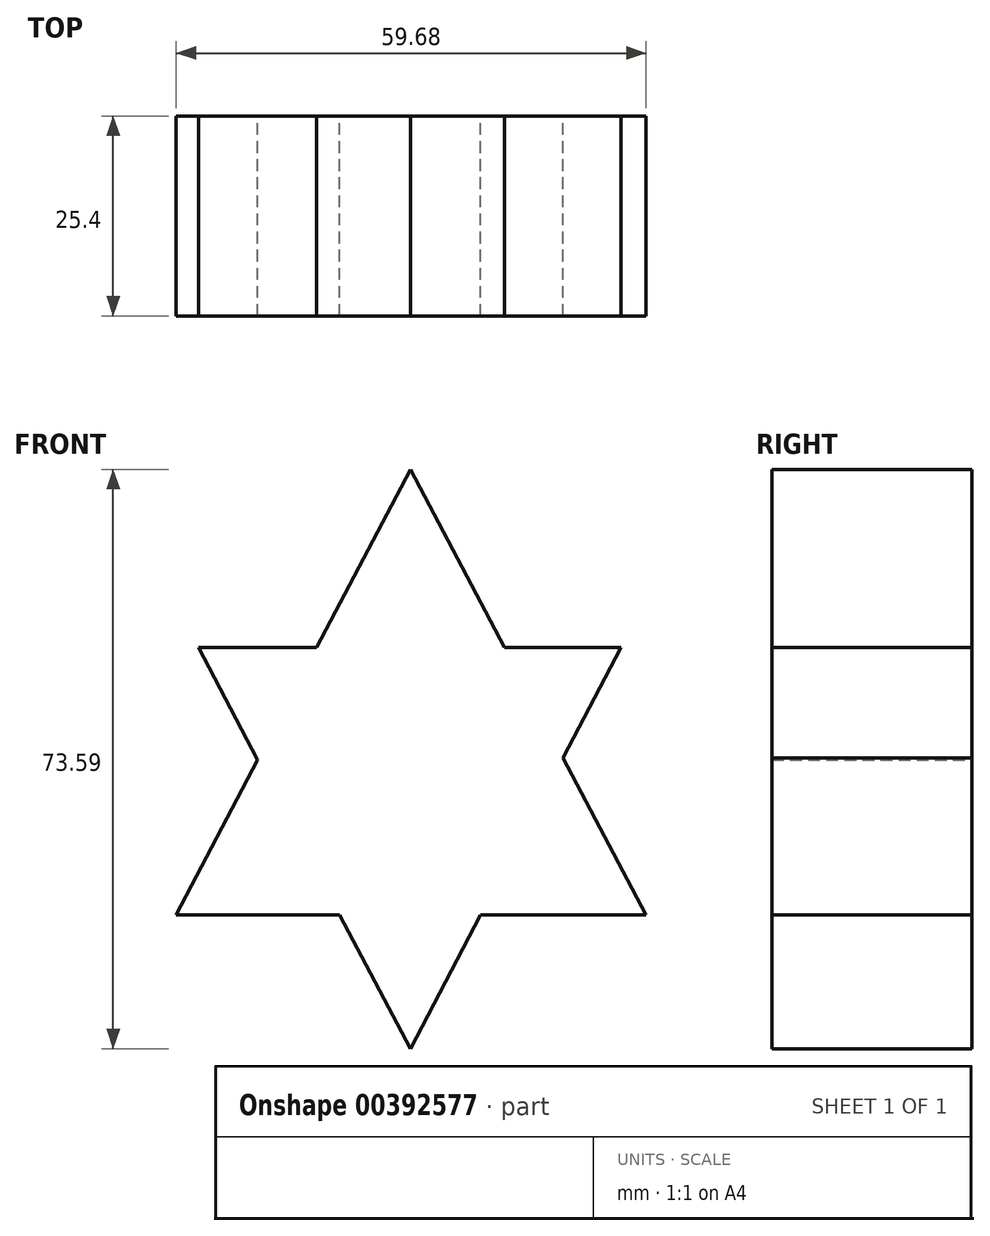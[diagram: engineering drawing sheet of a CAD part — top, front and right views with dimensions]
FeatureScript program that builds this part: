
annotation { "Feature Type Name" : "Feature", "Feature Type Description" : "" }
export const myFeature = defineFeature(function(context is Context, id is Id, definition is map)
    precondition{}
    {
        {
            var Q0;
            Q0=qCreatedBy(makeId("Front.planeOp"),FACE);
            var sketch = newSketch(context, id + "F0", { "sketchPlane" : qUnion([Q0])});
            skLineSegment(sketch, "E0", {"start": v(-29.75, 0) * mm, "end": v(0, 56.61) * mm});
            skLineSegment(sketch, "E1", {"start": v(0, 56.61) * mm, "end": v(29.93, 0) * mm});
            skLineSegment(sketch, "E2", {"start": v(29.93, 0) * mm, "end": v(-29.75, 0) * mm});
            skLineSegment(sketch, "E3", {"start": v(26.77, 33.96) * mm, "end": v(-26.93, 33.96) * mm});
            skLineSegment(sketch, "E4", {"start": v(0, -16.98) * mm, "end": v(26.77, 33.96) * mm});
            skLineSegment(sketch, "E5", {"start": v(-26.93, 33.96) * mm, "end": v(0, -16.98) * mm});
            skSolve(sketch);
        }
        {
            var Q0;
            Q0 = qSketchRegion(id + "F0", true);
            extrude(context, id + "F1", {"entities" : qUnion([Q0]), "depth" : 25.4 * mm});
        }
    });
